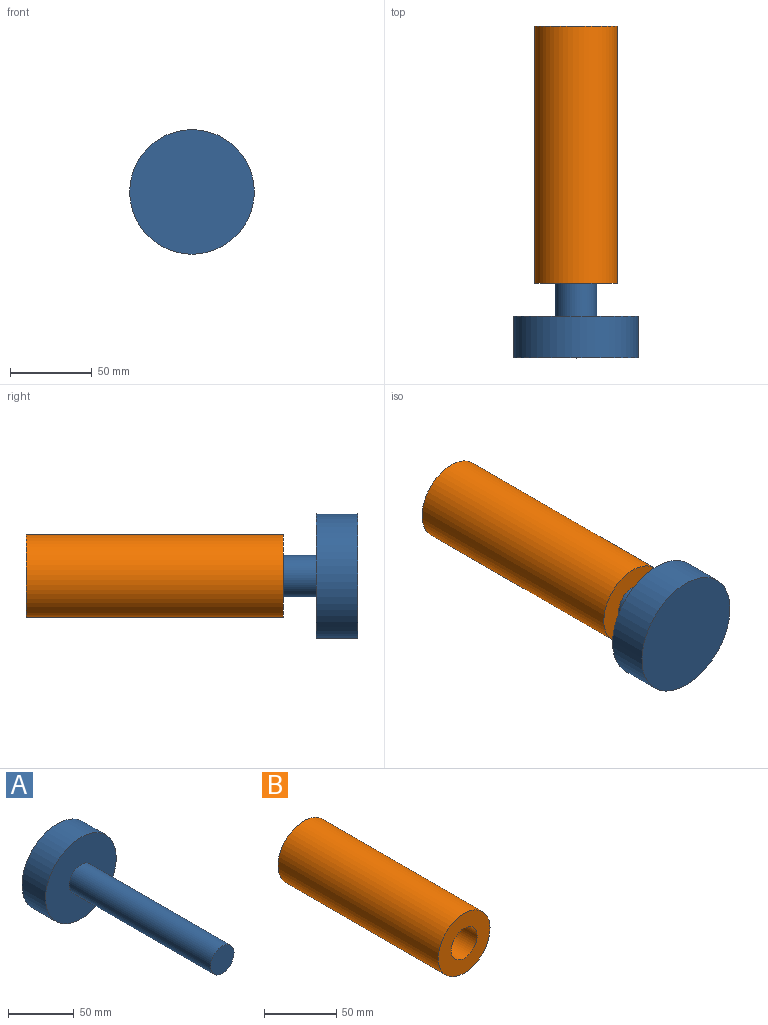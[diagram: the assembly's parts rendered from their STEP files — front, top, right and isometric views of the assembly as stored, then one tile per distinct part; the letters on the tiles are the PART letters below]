
ASSEMBLY  parts=2 mates=1
PART A: 5 faces, bbox 76.2x177.8x76.2 mm
  f0: cylinder r=12.7mm len=152.4mm, axis (0,1,0), area 12161mm2, adj f1,f3
  f1: plane 25.4x25.4mm, normal (0,-1,0), area 506.7mm2, adj f0
  f2: cylinder r=38.1mm len=76.2mm, axis (0,1,0), area 6080.5mm2, adj f3,f4
  f3: plane 76.2x76.2mm, normal (0,-1,0), area 4053.7mm2, adj f0,f2
  f4: plane 76.2x76.2mm, normal (0,1,0), area 4560.4mm2, adj f2
PART B: 5 faces, bbox 50.8x157.4x50.8 mm
  f0: cylinder r=12.7mm len=131.95mm, axis (0,1,0), area 10529.4mm2, adj f2,f4
  f1: cylinder r=25.4mm len=157.35mm, axis (0,1,0), area 25112.5mm2, adj f2,f3
  f2: plane 50.8x50.8mm, normal (0,-1,0), area 1520.1mm2, adj f0,f1
  f3: plane 50.8x50.8mm, normal (0,1,0), area 2026.8mm2, adj f1
  f4: plane 25.4x25.4mm, normal (0,-1,0), area 506.7mm2, adj f0
PLACE A rot(axis=(0,0,1),180deg) t=(-59.39,-84.6,128.98)mm
PLACE B t=(-59.39,118.45,128.98)mm
MATE slider A.f2 <-> B.f0  axis (0,-1,0) through (-59.39,-84.6,128.98)mm
